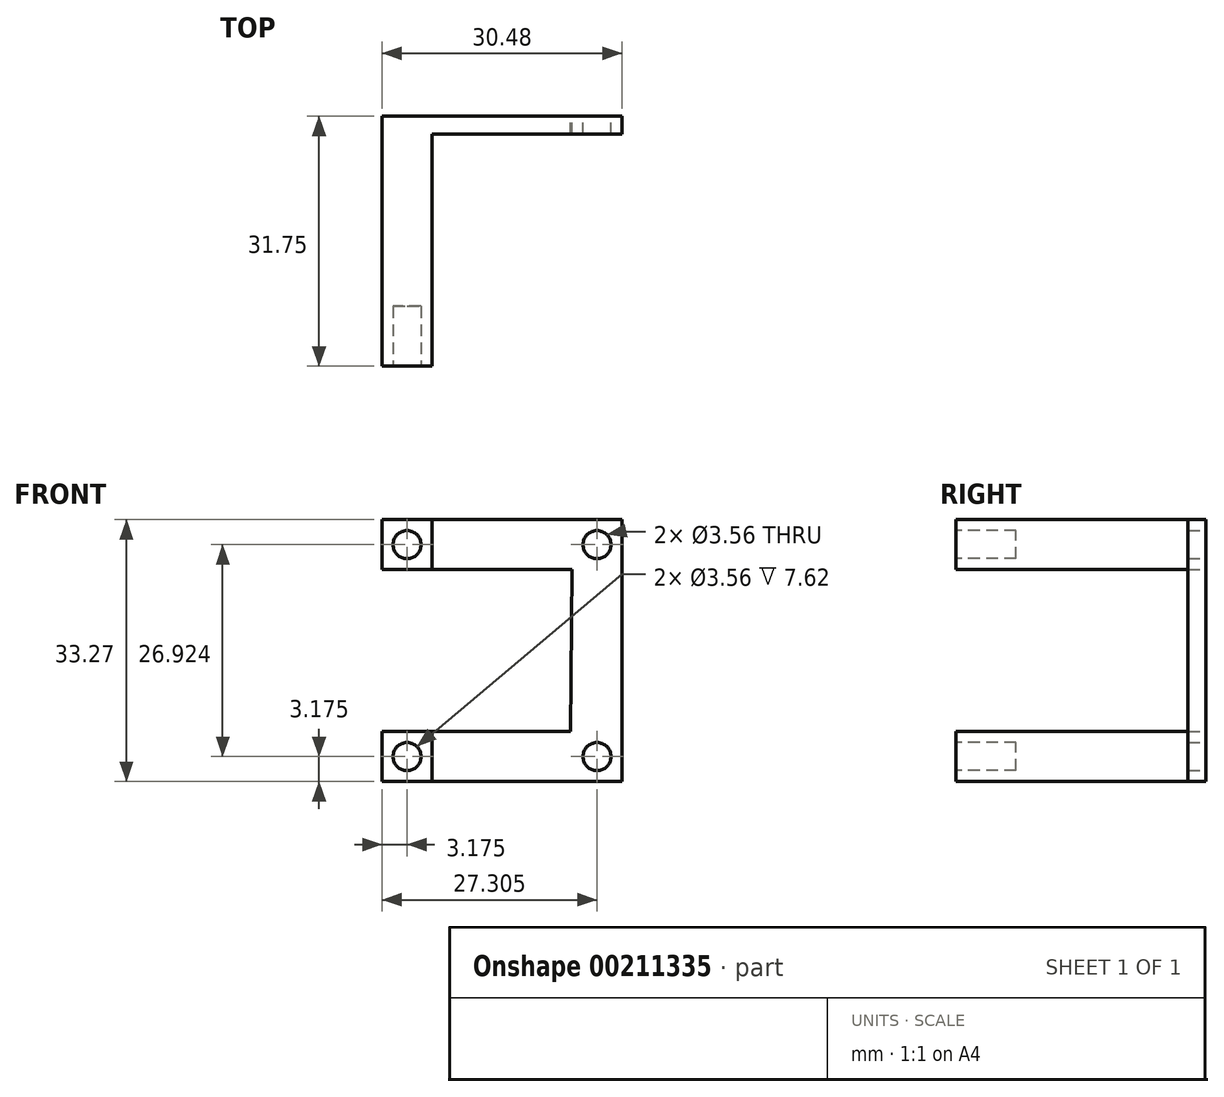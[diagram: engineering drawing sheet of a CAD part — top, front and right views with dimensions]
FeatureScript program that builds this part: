
annotation { "Feature Type Name" : "Feature", "Feature Type Description" : "" }
export const myFeature = defineFeature(function(context is Context, id is Id, definition is map)
    precondition{}
    {
        {
            var Q0;
            Q0=qCreatedBy(makeId("Front.planeOp"),FACE);
            var sketch = newSketch(context, id + "F0", { "sketchPlane" : qUnion([Q0])});
            skLineSegment(sketch, "E0.bottom", {"start": v(0, 0) * mm, "end": v(30.48, 0) * mm});
            skLineSegment(sketch, "E0.top", {"start": v(0, 33.27) * mm, "end": v(30.48, 33.27) * mm});
            skLineSegment(sketch, "E0.left", {"start": v(0, 0) * mm, "end": v(0, 6.35) * mm});
            skLineSegment(sketch, "E0.right", {"start": v(30.48, 0) * mm, "end": v(30.48, 33.27) * mm});
            skCircle(sketch, "E1", {"center": v(27.3, 3.18) * mm, "radius": 1.78 * mm});
            skCircle(sketch, "E2", {"center": v(27.3, 30.1) * mm, "radius": 1.78 * mm});
            skCircle(sketch, "E3", {"center": v(3.17, 3.18) * mm, "radius": 177.8 * mm});
            skLineSegment(sketch, "E4", {"start": v(0, 26.92) * mm, "end": v(24.1, 26.92) * mm});
            skLineSegment(sketch, "E5", {"start": v(24.1, 26.92) * mm, "end": v(23.94, 6.35) * mm});
            skLineSegment(sketch, "E6", {"start": v(0, 16.64) * mm, "end": v(30.48, 16.64) * mm, "construction": true});
            skLineSegment(sketch, "E7.MirrorCS", {"start": v(0, 6.35) * mm, "end": v(24.1, 6.35) * mm});
            skLineSegment(sketch, "E8.trimOffspring", {"start": v(23.89, 0) * mm, "end": v(23.89, -0.1) * mm});
            skLineSegment(sketch, "E9.trimOffspring", {"start": v(0, 26.92) * mm, "end": v(0, 33.27) * mm});
            skSolve(sketch);
        }
        {
            var Q0;
            Q0=makeQuery(id+"F0.imprint","IMPRINT",FACE,{"disambiguationData":[TD([[makeQuery(id+"F0.imprint","IMPRINT",EDGE,{"derivedFrom":sQuery(id+"F0.wireOp",EDGE,"E0.bottom")}),1.0]])]});
            extrude(context, id + "F1", {"entities" : qUnion([Q0]), "depth" : 2.3 * mm});
        }
        {
            var Q0;
            Q0=makeQuery(id+"F1.opExtrude","CAP_FACE",FACE,{"disambiguationData":[OSD([sQuery(id+"F0.wireOp",EDGE,"E0.bottom"),sQuery(id+"F0.wireOp",EDGE,"E0.top"),sQuery(id+"F0.wireOp",EDGE,"E0.left"),sQuery(id+"F0.wireOp",EDGE,"E0.right"),sQuery(id+"F0.wireOp",EDGE,"E1"),sQuery(id+"F0.wireOp",EDGE,"E2")])],"isStart":false});
            var sketch = newSketch(context, id + "F2", { "sketchPlane" : qUnion([Q0])});
            skLineSegment(sketch, "E10", {"start": v(27.3, 3.18) * mm, "end": v(17.74, 2.47) * mm, "construction": true});
            skLineSegment(sketch, "E11", {"start": v(30.48, 16.64) * mm, "end": v(-0.81, 16.64) * mm, "construction": true});
            skLineSegment(sketch, "E12.left", {"start": v(0, 0) * mm, "end": v(0, 0) * mm});
            skLineSegment(sketch, "E13.bottom", {"start": v(0, 26.92) * mm, "end": v(6.35, 26.92) * mm});
            skLineSegment(sketch, "E13.top", {"start": v(0, 33.27) * mm, "end": v(6.35, 33.27) * mm});
            skLineSegment(sketch, "E13.left", {"start": v(0, 26.92) * mm, "end": v(0, 33.27) * mm});
            skLineSegment(sketch, "E13.right", {"start": v(6.35, 26.92) * mm, "end": v(6.35, 33.27) * mm});
            skLineSegment(sketch, "E14.bottom", {"start": v(0, 0) * mm, "end": v(6.35, 0) * mm});
            skLineSegment(sketch, "E14.top", {"start": v(0, 6.35) * mm, "end": v(6.35, 6.35) * mm});
            skLineSegment(sketch, "E14.left", {"start": v(0, 0) * mm, "end": v(0, 6.35) * mm});
            skLineSegment(sketch, "E14.right", {"start": v(6.35, 0) * mm, "end": v(6.35, 6.35) * mm});
            skSolve(sketch);
        }
        {
            var Q0;
            Q0 = qSketchRegion(id + "F2", true);
            extrude(context, id + "F3", {"entities" : qUnion([Q0]), "operationType" : NewBodyOperationType.ADD, "depth" : 29.46 * mm});
        }
        {
            var Q0;
            Q0=makeQuery(id+"F3.opExtrude","CAP_FACE",FACE,{"disambiguationData":[OSD([sQuery(id+"F2.wireOp",EDGE,"E13.bottom"),sQuery(id+"F2.wireOp",EDGE,"E13.top"),sQuery(id+"F2.wireOp",EDGE,"E13.left"),sQuery(id+"F2.wireOp",EDGE,"E13.right")])],"isStart":false});
            var sketch = newSketch(context, id + "F4", { "sketchPlane" : qUnion([Q0])});
            skCircle(sketch, "E15", {"center": v(3.17, 30.1) * mm, "radius": 1.78 * mm});
            skPoint(sketch, "E15.centerSnap0", {"position": v(3.17, 33.27) * mm});
            skCircle(sketch, "E16", {"center": v(3.17, 3.17) * mm, "radius": 1.78 * mm});
            skSolve(sketch);
        }
        {
            var Q0;
            Q0 = qSketchRegion(id + "F4", true);
            extrude(context, id + "F5", {"entities" : qUnion([Q0]), "operationType" : NewBodyOperationType.REMOVE, "oppositeDirection" : true, "depth" : 7.62 * mm});
        }
    });
